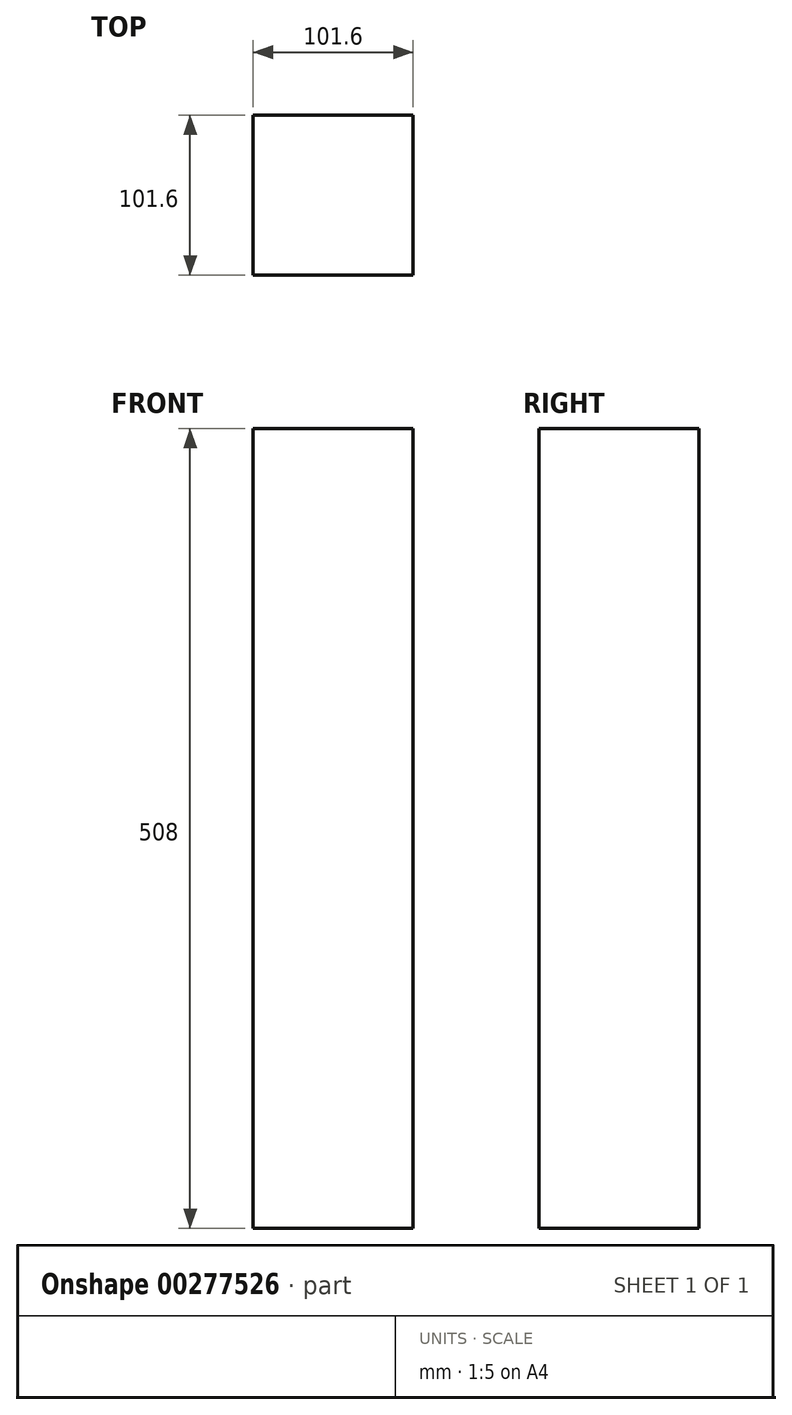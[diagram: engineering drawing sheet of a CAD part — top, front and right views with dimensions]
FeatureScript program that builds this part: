
annotation { "Feature Type Name" : "Feature", "Feature Type Description" : "" }
export const myFeature = defineFeature(function(context is Context, id is Id, definition is map)
    precondition{}
    {
        {
            var Q0;
            Q0=qCreatedBy(makeId("Top.planeOp"),FACE);
            var sketch = newSketch(context, id + "F0", { "sketchPlane" : qUnion([Q0])});
            skLineSegment(sketch, "E0.bottom", {"start": v(-50.8, 50.8) * mm, "end": v(50.8, 50.8) * mm});
            skLineSegment(sketch, "E0.top", {"start": v(-50.8, -50.8) * mm, "end": v(50.8, -50.8) * mm});
            skLineSegment(sketch, "E0.left", {"start": v(-50.8, 50.8) * mm, "end": v(-50.8, -50.8) * mm});
            skLineSegment(sketch, "E0.right", {"start": v(50.8, 50.8) * mm, "end": v(50.8, -50.8) * mm});
            skPoint(sketch, "E0.middle", {"position": v(0, 0) * mm});
            skSolve(sketch);
        }
        {
            var Q0;
            Q0=makeQuery(id+"F0.imprint","IMPRINT",FACE,{"disambiguationData":[TD([[makeQuery(id+"F0.imprint","IMPRINT",EDGE,{"derivedFrom":sQuery(id+"F0.wireOp",EDGE,"E0.bottom")}),-1.0]])]});
            extrude(context, id + "F1", {"entities" : qUnion([Q0]), "depth" : 508 * mm});
        }
    });
